# Revit family: Shower-Bath_and_Shower_Trim-KOHLER-Venza-K-TLS28127
name_source: partatom
category: Plumbing Fixtures
units: mm (PartAtom-declared; Revit-internal decimal feet)

## family parameters
Cut with Voids When Loaded = No
Host = Face
OmniClass Number = 23.31.17.00
OmniClass Title = Showers
Part Type = Normal
Room Calculation Point = No
Round Connector Dimension = Use Diameter
Shared = No

## types (3) — shared parameters
ADA Compliant = No
Assembly Code = D2010700
CW Connection = No
Cold Water Inlet = Cold Water Inlet
Date Modified = 12/23/2023
Default Elevation = 42"
Description = Rite Temp Pressure Balancing Bath/Shower Trim Less Head
Drain Included = No
Flow Rate = 0 GPM
HW Connection = Yes
Handle Clearance = 3 3/16"
Height = 6 1/2"
Hot Water Inlet = Hot Water Inlet
Length = 5 13/16"
Manufacturer = Kohler Co.
Master Format 2014 = 22 42 23
Master Format 2014 Name = Residential Showers
Material = Premium Metal Construction
Pressure = 0.00 psi
Product Documentation Link = https://www.us.kohler.com
Product Name = Venza
Product Page URL = http://www.us.kohler.com
Spout Reach = 5 3/16"
Tempered Water Inlet 1 = Tempered Water Inlet 1
Tempered Water Inlet 2 = Tempered Water Inlet 2
URL = https://www.us.kohler.com
Vent Connection = No
Waste Connection = No
Waste Water Outlet = Waste Water Outlet
WaterSense Certified = No
Width = 6 1/2"

## per-type parameters (varying)
| type | Finish | Model | Type |
| BL-Matte Black | Kohler-Metal-BL-Matte_Black | K-TLS28127-4-BL | 1 |
| BN-Vibrant Brushed Nickel | Kohler-Metal-BN-Vibrant_Brushed_Nickel | K-TLS28127-4-BN | 2 |
| CP-Polished Chrome | Kohler-Metal-CP-Polished_Chrome | K-TLS28127-4-CP | 3 |

## geometry (parser evidence)
native form markers: Sweep x14
no freeform markers — native parametric forms only
